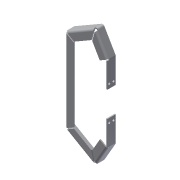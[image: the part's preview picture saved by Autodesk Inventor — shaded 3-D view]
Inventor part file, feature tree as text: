
AUTODESK INVENTOR PART (.ipt)
format: ipt  version: 2015 (Build 190159000, 159)  size: 296,448 bytes
history: native  units: in
note: dims shown in document units (in); Inventor stores cm internally (conversion verified against a paired STEP export)
features: sheet_metal_op x6, other x3, sketch x2, hole x1, reference x1
ambient origin geometry x8: Origin, YZ Plane, XZ Plane, XY Plane, X Axis, Y Axis, Z Axis, Center Point
bodies: Solid1 (feature_tree)
feature tree (13):
  sheet_metal_op  "Contour Flange1"
  sheet_metal_op  "Flange2"
  hole  "Hole1"  [1 undecoded]
  reference  "Reference1"
  other  "Plate1"
  sheet_metal_op  "Bend1"
  sheet_metal_op  "Corner1"
  sketch  "Sketch3"  dims[d0=120.0deg d2=5.0in]
  other  "Plate3"
  sheet_metal_op  "Bend3"
  sheet_metal_op  "Corner3"
  sketch  "Sketch4"  dims[d3=3.0in d4=0.125in d5=0.0625in d6=0.25in d7=0.125in d8=1.0in d9=0.125in d10=0.125in d11=0.5in d12=0.125in d13=0.125in d24=0.125in d25=0.0625in d26=0.25in d27=0.125in d28=1.0in d29=90.0deg d30=0.125in d31=0.5in d32=0.125in d33=0.125in d34=0.25in d35=0.75in d36=0.375in d37=0.25in d38=0.5635in d39=0.125in d40=0.8108in d43=1.47in]
  other  "Definition1"
note: 1 required parameter value undecoded (feature->parameter linkage not recoverable at this tier; creation-order binding heuristic only, values carry confidence <= 0.55)
